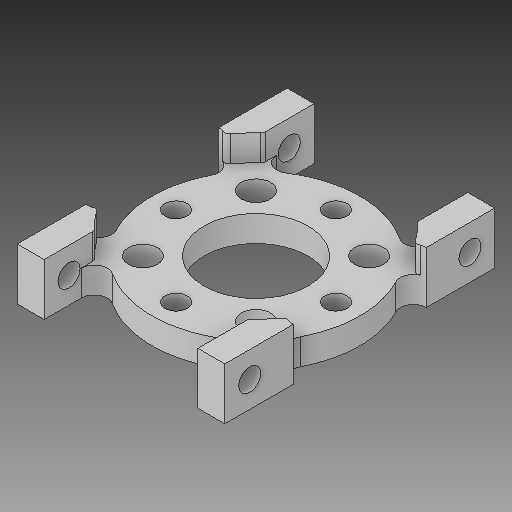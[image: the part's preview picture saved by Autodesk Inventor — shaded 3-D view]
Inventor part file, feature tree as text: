
AUTODESK INVENTOR PART (.ipt)
format: ipt  version: 2017 (Build 210142000, 142)  size: 189,440 bytes
history: native  units: in
note: dims shown in document units (in); Inventor stores cm internally (conversion verified against a paired STEP export)
features: mirror x1
ambient origin geometry x8: Origin, YZ Plane, XZ Plane, XY Plane, X Axis, Y Axis, Z Axis, Center Point
bodies: Solid1 (feature_tree)
feature tree (1):
  mirror  "Mirror6"
